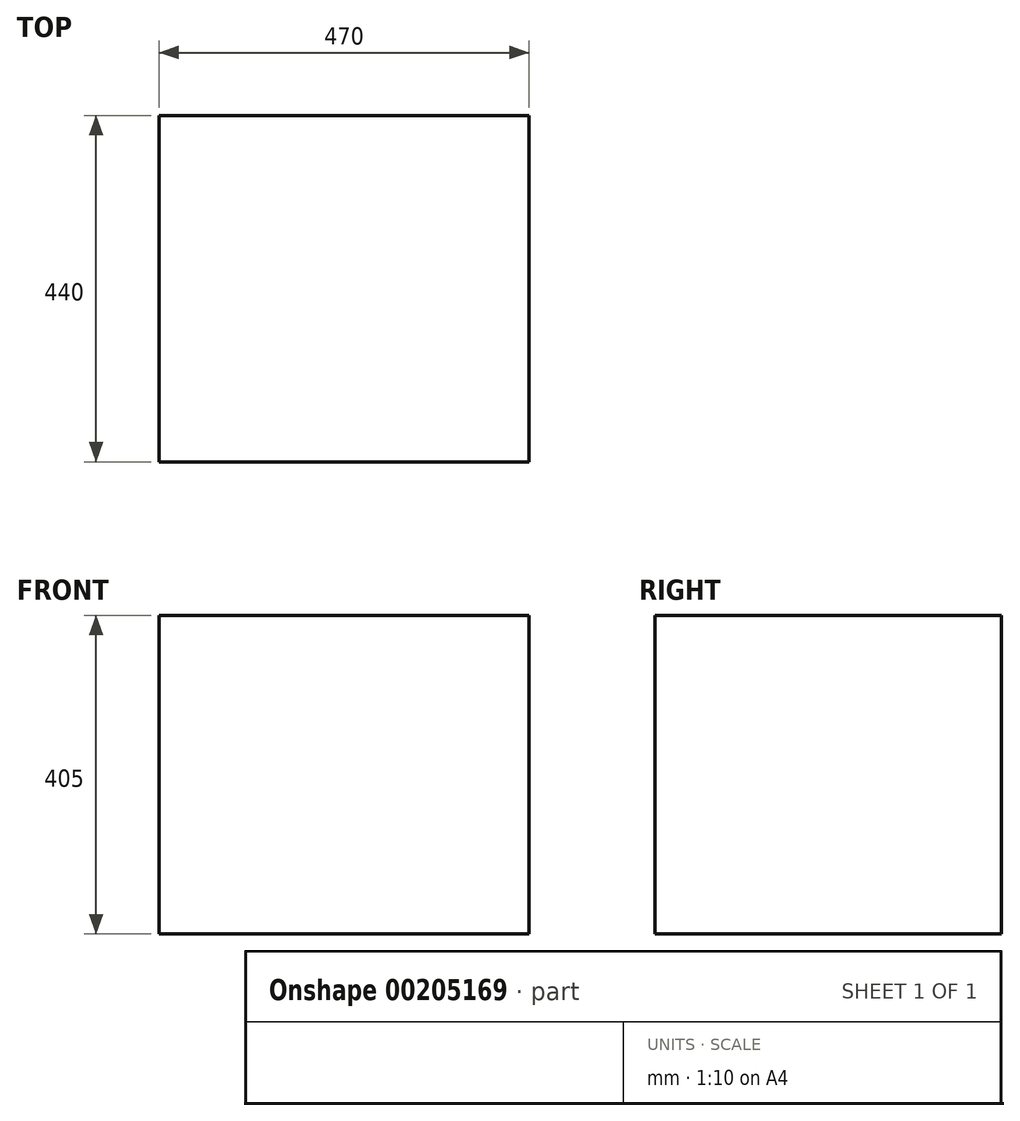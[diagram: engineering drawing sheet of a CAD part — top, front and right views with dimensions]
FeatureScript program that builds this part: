
annotation { "Feature Type Name" : "Feature", "Feature Type Description" : "" }
export const myFeature = defineFeature(function(context is Context, id is Id, definition is map)
    precondition{}
    {
        {
            var Q0;
            Q0=qCreatedBy(makeId("Top.planeOp"),FACE);
            var sketch = newSketch(context, id + "F0", { "sketchPlane" : qUnion([Q0])});
            skLineSegment(sketch, "E0.bottom", {"start": v(0, 0) * mm, "end": v(-470, 0) * mm});
            skLineSegment(sketch, "E0.top", {"start": v(0, -440) * mm, "end": v(-470, -440) * mm});
            skLineSegment(sketch, "E0.left", {"start": v(0, 0) * mm, "end": v(0, -440) * mm});
            skLineSegment(sketch, "E0.right", {"start": v(-470, 0) * mm, "end": v(-470, -440) * mm});
            skSolve(sketch);
        }
        {
            var Q0;
            Q0 = qSketchRegion(id + "F0", true);
            extrude(context, id + "F1", {"entities" : qUnion([Q0]), "depth" : 405 * mm});
        }
    });
